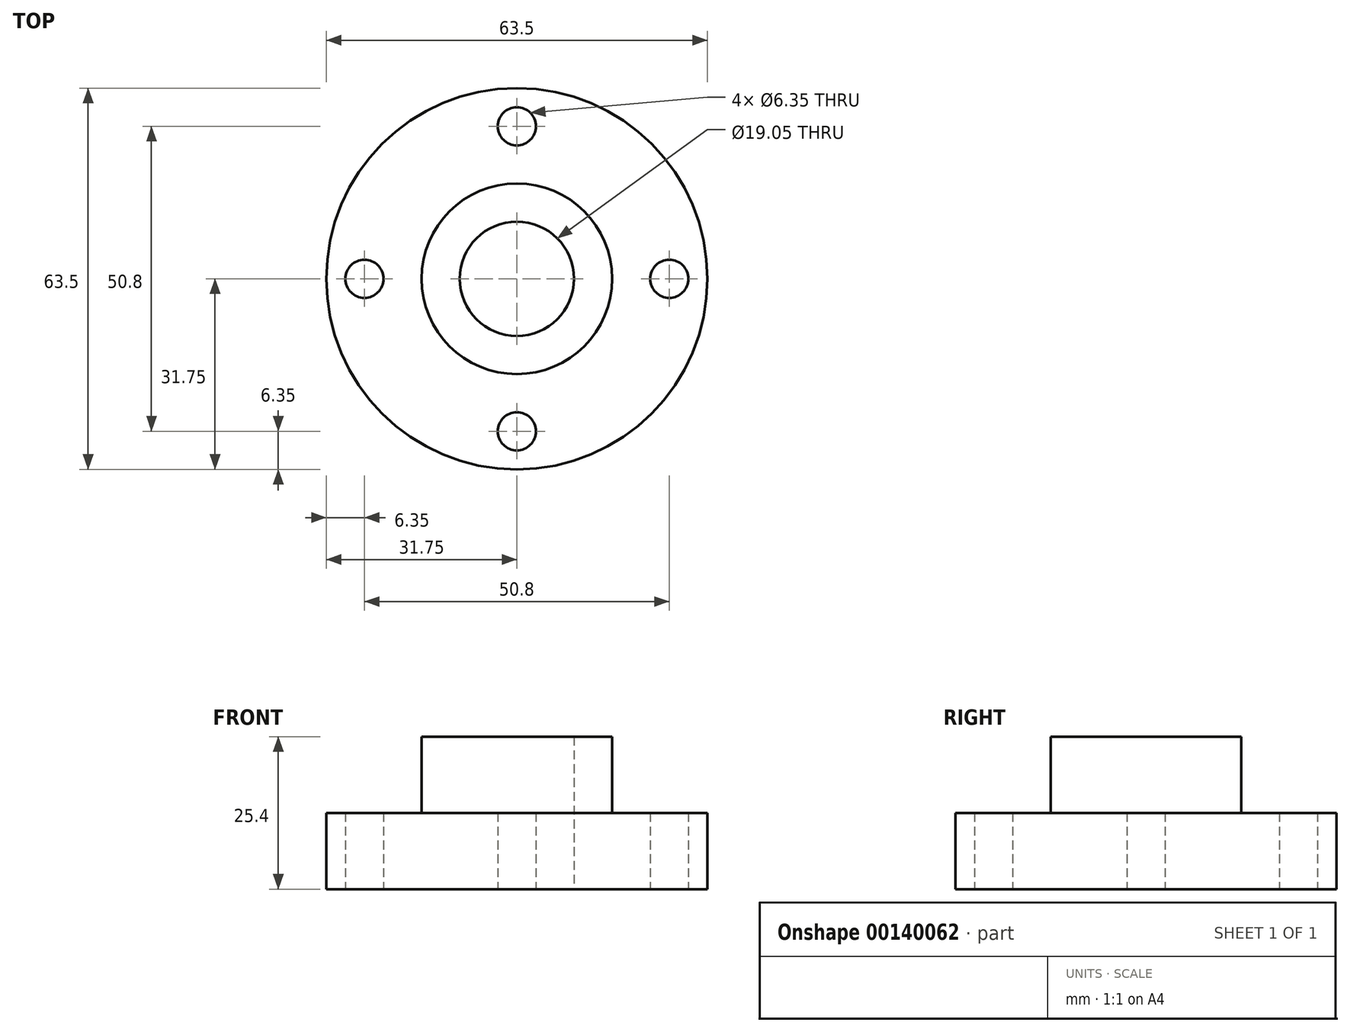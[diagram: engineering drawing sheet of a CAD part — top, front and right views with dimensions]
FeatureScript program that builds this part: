
annotation { "Feature Type Name" : "Feature", "Feature Type Description" : "" }
export const myFeature = defineFeature(function(context is Context, id is Id, definition is map)
    precondition{}
    {
        {
            var Q0;
            Q0=qCreatedBy(makeId("Top.planeOp"),FACE);
            var sketch = newSketch(context, id + "F0", { "sketchPlane" : qUnion([Q0])});
            skCircle(sketch, "E0", {"center": v(0, 0) * mm, "radius": 31.75 * mm});
            skCircle(sketch, "E1", {"center": v(0, 0) * mm, "radius": 15.88 * mm});
            skCircle(sketch, "E2", {"center": v(0, 0) * mm, "radius": 9.53 * mm});
            skCircle(sketch, "E3", {"center": v(0, 0) * mm, "radius": 25.4 * mm, "construction": true});
            skCircle(sketch, "E4", {"center": v(0, 25.4) * mm, "radius": 3.18 * mm});
            skCircle(sketch, "E5.1.0", {"center": v(-25.4, 0) * mm, "radius": 3.18 * mm});
            skCircle(sketch, "E5.2.0", {"center": v(0, -25.4) * mm, "radius": 3.18 * mm});
            skCircle(sketch, "E5.3.0", {"center": v(25.4, 0) * mm, "radius": 3.18 * mm});
            skSolve(sketch);
        }
        {
            var Q0;
            Q0=makeQuery(id+"F0.imprint","IMPRINT",FACE,{"disambiguationData":[TD([[makeQuery(id+"F0.imprint","IMPRINT",EDGE,{"derivedFrom":sQuery(id+"F0.wireOp",EDGE,"E0")}),1.0]])]});
            extrude(context, id + "F1", {"entities" : qUnion([Q0]), "depth" : 12.7 * mm});
        }
        {
            var Q0;
            Q0=makeQuery(id+"F0.imprint","IMPRINT",FACE,{"disambiguationData":[TD([[makeQuery(id+"F0.imprint","IMPRINT",EDGE,{"derivedFrom":sQuery(id+"F0.wireOp",EDGE,"E1")}),1.0]])]});
            extrude(context, id + "F2", {"entities" : qUnion([Q0]), "operationType" : NewBodyOperationType.ADD, "depth" : 25.4 * mm});
        }
    });
